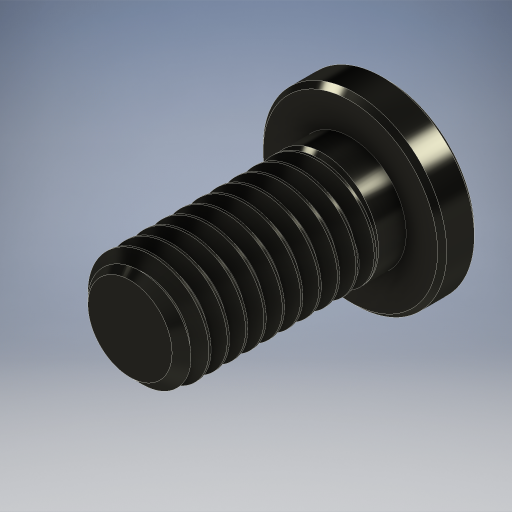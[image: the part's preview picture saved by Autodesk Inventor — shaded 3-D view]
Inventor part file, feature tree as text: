
AUTODESK INVENTOR PART (.ipt)
format: ipt  version: 2024 (Build 280153000, 153)  size: 701,440 bytes
history: native  units: in
note: dims shown in document units (in); Inventor stores cm internally (conversion verified against a paired STEP export)
features: revolve x1
ambient origin geometry x8: Origin, YZ Plane, XZ Plane, XY Plane, X Axis, Y Axis, Z Axis, Center Point
bodies: Solid1 (feature_tree)
feature tree (1):
  revolve  "Revolve1"  [1 undecoded]
note: 1 required parameter value undecoded (feature->parameter linkage not recoverable at this tier; creation-order binding heuristic only, values carry confidence <= 0.55)
